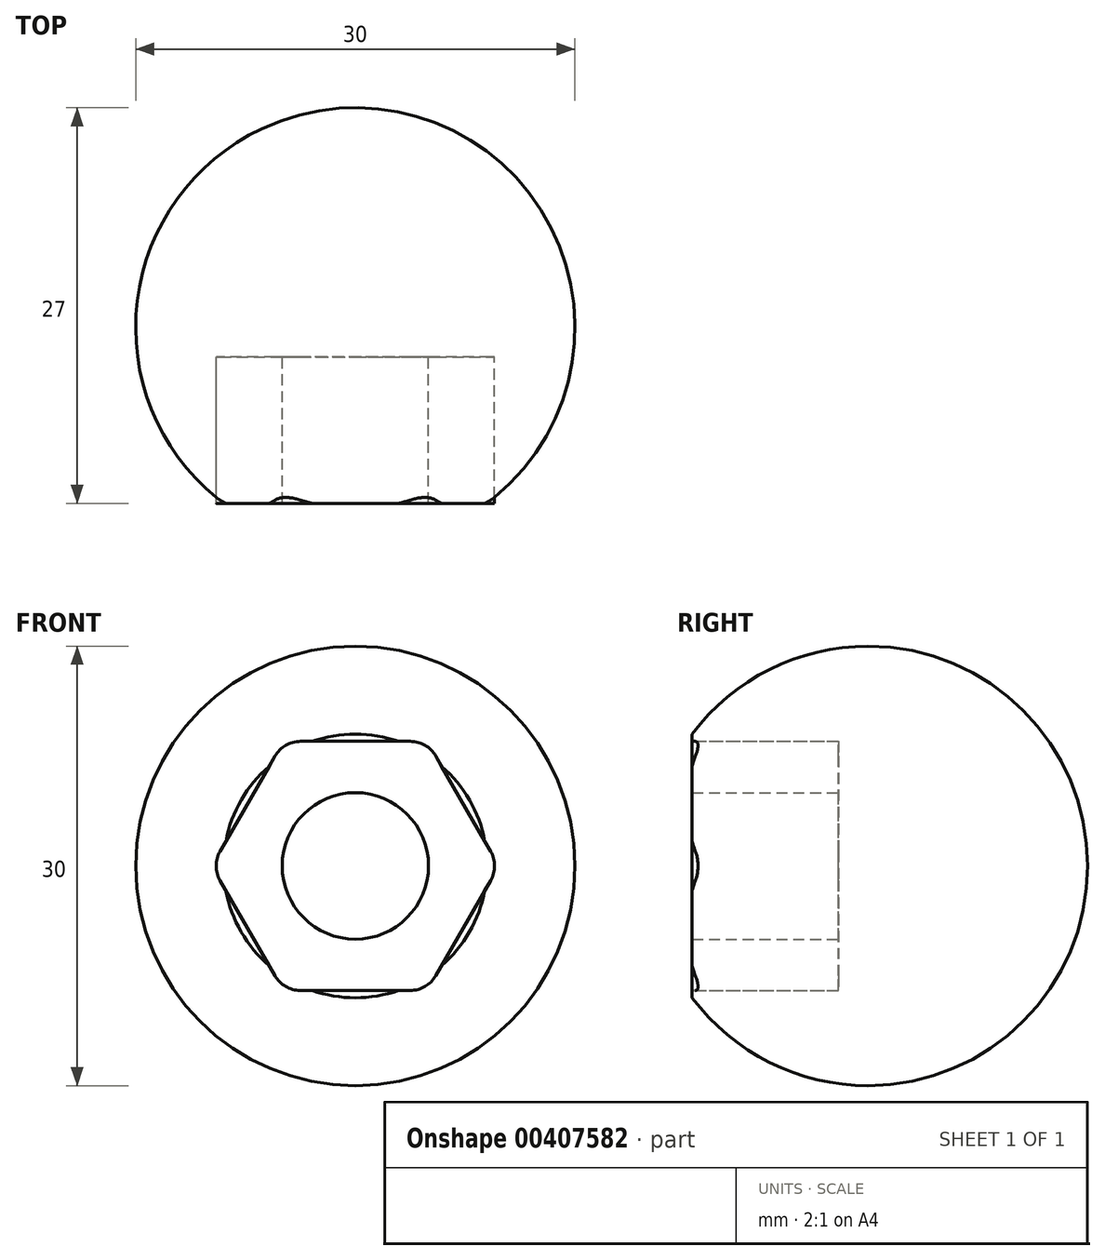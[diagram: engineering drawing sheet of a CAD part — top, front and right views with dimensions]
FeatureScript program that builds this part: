
annotation { "Feature Type Name" : "Feature", "Feature Type Description" : "" }
export const myFeature = defineFeature(function(context is Context, id is Id, definition is map)
    precondition{}
    {
        {
            var Q0;
            Q0=qCreatedBy(makeId("Front.planeOp"),FACE);
            var sketch = newSketch(context, id + "F0", { "sketchPlane" : qUnion([Q0])});
            skLineSegment(sketch, "E0", {"start": v(0, 17.98) * mm, "end": v(0, -21.13) * mm, "construction": true});
            skArc(sketch, "E1", {"start": v(0, 15) * mm, "mid": v(-15, 0) * mm, "end": v(0, -15) * mm});
            skLineSegment(sketch, "E2", {"start": v(0, -15) * mm, "end": v(0, 15) * mm});
            skSolve(sketch);
        }
        {
            var Q0;
            Q0=makeQuery(id+"F0.imprint","IMPRINT",FACE,{"disambiguationData":[TD([[makeQuery(id+"F0.imprint","IMPRINT",EDGE,{"derivedFrom":sQuery(id+"F0.wireOp",EDGE,"E1")}),1.0]])]});
            var Q1;
            Q1=sQuery(id+"F0.wireOp",EDGE,"E0");
            revolve(context, id + "F1", {"surfaceOperationType" : NewSurfaceOperationType.NEW, "entities" : qUnion([Q0]), "axis" : qUnion([Q1]), "revolveType" : RevolveType.FULL});
        }
        {
            var Q0;
            Q0=qCreatedBy(makeId("Front.planeOp"),FACE);
            var sketch = newSketch(context, id + "F2", { "sketchPlane" : qUnion([Q0])});
            skCircle(sketch, "E3.cCircle", {"center": v(0, 0) * mm, "radius": 8.5 * mm, "construction": true});
            skLineSegment(sketch, "E3.0", {"start": v(5.49, 7.5) * mm, "end": v(9.24, 1) * mm});
            skLineSegment(sketch, "E3.1", {"start": v(9.24, -1) * mm, "end": v(5.48, -7.5) * mm});
            skLineSegment(sketch, "E3.2", {"start": v(3.75, -8.5) * mm, "end": v(-3.76, -8.5) * mm});
            skLineSegment(sketch, "E3.3", {"start": v(-5.49, -7.5) * mm, "end": v(-9.24, -1) * mm});
            skLineSegment(sketch, "E3.4", {"start": v(-9.24, 1) * mm, "end": v(-5.48, 7.5) * mm});
            skLineSegment(sketch, "E3.5", {"start": v(-3.75, 8.5) * mm, "end": v(3.76, 8.5) * mm});
            skPoint(sketch, "E3.0.midPoint", {"position": v(7.36, 4.25) * mm});
            skCircle(sketch, "E4", {"center": v(0, 0) * mm, "radius": 5 * mm});
            skPoint(sketch, "E5.visualSharp", {"position": v(-4.9, 8.5) * mm});
            skArc(sketch, "E5.filletArc", {"start": v(-3.75, 8.5) * mm, "mid": v(-4.75, 8.23) * mm, "end": v(-5.48, 7.5) * mm});
            skPoint(sketch, "E6.visualSharp", {"position": v(4.91, 8.5) * mm});
            skArc(sketch, "E6.filletArc", {"start": v(5.49, 7.5) * mm, "mid": v(4.76, 8.23) * mm, "end": v(3.76, 8.5) * mm});
            skPoint(sketch, "E7.visualSharp", {"position": v(9.81, 0) * mm});
            skArc(sketch, "E7.filletArc", {"start": v(9.24, -1) * mm, "mid": v(9.5, 0) * mm, "end": v(9.24, 1) * mm});
            skPoint(sketch, "E8.visualSharp", {"position": v(4.9, -8.5) * mm});
            skArc(sketch, "E8.filletArc", {"start": v(3.75, -8.5) * mm, "mid": v(4.75, -8.23) * mm, "end": v(5.48, -7.5) * mm});
            skPoint(sketch, "E9.visualSharp", {"position": v(-4.91, -8.5) * mm});
            skArc(sketch, "E9.filletArc", {"start": v(-5.49, -7.5) * mm, "mid": v(-4.76, -8.23) * mm, "end": v(-3.76, -8.5) * mm});
            skPoint(sketch, "E10.visualSharp", {"position": v(-9.81, 0) * mm});
            skArc(sketch, "E10.filletArc", {"start": v(-9.24, 1) * mm, "mid": v(-9.5, 0) * mm, "end": v(-9.24, -1) * mm});
            skSolve(sketch);
        }
        {
            var Q0;
            Q0=makeQuery(id+"F2.imprint","IMPRINT",FACE,{"disambiguationData":[TD([[makeQuery(id+"F2.imprint","IMPRINT",EDGE,{"derivedFrom":sQuery(id+"F2.wireOp",EDGE,"E3.0")}),-1.0]])]});
            extrude(context, id + "F3", {"entities" : qUnion([Q0]), "depth" : 12 * mm, "offsetDistance" : 25 * mm, "hasSecondDirection" : true, "secondDirectionOppositeDirection" : false, "secondDirectionDepth" : 2 * mm});
        }
        {
            var Q0;
            Q0=makeQuery(id+"F3.opExtrude","CAP_FACE",FACE,{"disambiguationData":[OSD([sQuery(id+"F2.wireOp",EDGE,"E3.0"),sQuery(id+"F2.wireOp",EDGE,"E3.1"),sQuery(id+"F2.wireOp",EDGE,"E3.2"),sQuery(id+"F2.wireOp",EDGE,"E3.3"),sQuery(id+"F2.wireOp",EDGE,"E3.4"),sQuery(id+"F2.wireOp",EDGE,"E3.5"),sQuery(id+"F2.wireOp",EDGE,"E4"),sQuery(id+"F2.wireOp",EDGE,"E5.filletArc"),sQuery(id+"F2.wireOp",EDGE,"E6.filletArc"),sQuery(id+"F2.wireOp",EDGE,"E7.filletArc"),sQuery(id+"F2.wireOp",EDGE,"E8.filletArc"),sQuery(id+"F2.wireOp",EDGE,"E9.filletArc"),sQuery(id+"F2.wireOp",EDGE,"E10.filletArc")])],"isStart":false});
            var sketch = newSketch(context, id + "F4", { "sketchPlane" : qUnion([Q0])});
            skLineSegment(sketch, "E11.bottom", {"start": v(-22.5, 22.5) * mm, "end": v(22.5, 22.5) * mm});
            skLineSegment(sketch, "E11.top", {"start": v(-22.5, -22.5) * mm, "end": v(22.5, -22.5) * mm});
            skLineSegment(sketch, "E11.left", {"start": v(-22.5, 22.5) * mm, "end": v(-22.5, -22.5) * mm});
            skLineSegment(sketch, "E11.right", {"start": v(22.5, 22.5) * mm, "end": v(22.5, -22.5) * mm});
            skSolve(sketch);
        }
        {
            var Q0;
            Q0=makeQuery(id+"F4.imprint","IMPRINT",FACE,{"disambiguationData":[TD([[makeQuery(id+"F4.imprint","IMPRINT",EDGE,{"derivedFrom":sQuery(id+"F4.wireOp",EDGE,"E11.bottom")}),-1.0]])]});
            var Q1;
            Q1=makeQuery(id+"F4.imprint","IMPRINT",FACE,{"disambiguationData":[TD([[makeQuery(id+"F4.imprint","IMPRINT",EDGE,{"derivedFrom":makeQuery(id+"F3.opExtrude","CAP_EDGE",EDGE,{"disambiguationData":[OSD([sQuery(id+"F2.wireOp",EDGE,"E3.0")])],"isStart":false})}),-1.0]])]});
            extrude(context, id + "F5", {"entities" : qUnion([Q0, Q1]), "operationType" : NewBodyOperationType.REMOVE, "depth" : 25 * mm, "offsetDistance" : 25 * mm});
        }
        {
            var Q0;
            Q0=makeQuery(id+"F3.opExtrude","SWEPT_BODY",BODY,{"disambiguationData":[OSD([sQuery(id+"F2.wireOp",EDGE,"E3.0"),sQuery(id+"F2.wireOp",EDGE,"E3.1"),sQuery(id+"F2.wireOp",EDGE,"E3.2"),sQuery(id+"F2.wireOp",EDGE,"E3.3"),sQuery(id+"F2.wireOp",EDGE,"E3.4"),sQuery(id+"F2.wireOp",EDGE,"E3.5"),sQuery(id+"F2.wireOp",EDGE,"E4"),sQuery(id+"F2.wireOp",EDGE,"E5.filletArc"),sQuery(id+"F2.wireOp",EDGE,"E6.filletArc"),sQuery(id+"F2.wireOp",EDGE,"E7.filletArc"),sQuery(id+"F2.wireOp",EDGE,"E8.filletArc"),sQuery(id+"F2.wireOp",EDGE,"E9.filletArc"),sQuery(id+"F2.wireOp",EDGE,"E10.filletArc")])]});
            var Q1;
            Q1=makeQuery(id+"F1.opRevolve","SWEPT_BODY",BODY,{"disambiguationData":[OSD([sQuery(id+"F0.wireOp",EDGE,"E1"),sQuery(id+"F0.wireOp",EDGE,"E2")])]});
            booleanBodies(context, id + "F6", {"operationType" : BooleanOperationType.SUBTRACTION, "tools" : qUnion([Q0]), "targets" : qUnion([Q1]), "keepTools" : true});
        }
        {
            var Q0;
            Q0=makeQuery(id+"F3.opExtrude","CAP_FACE",FACE,{"disambiguationData":[OSD([sQuery(id+"F2.wireOp",EDGE,"E3.0"),sQuery(id+"F2.wireOp",EDGE,"E3.1"),sQuery(id+"F2.wireOp",EDGE,"E3.2"),sQuery(id+"F2.wireOp",EDGE,"E3.3"),sQuery(id+"F2.wireOp",EDGE,"E3.4"),sQuery(id+"F2.wireOp",EDGE,"E3.5"),sQuery(id+"F2.wireOp",EDGE,"E4"),sQuery(id+"F2.wireOp",EDGE,"E5.filletArc"),sQuery(id+"F2.wireOp",EDGE,"E6.filletArc"),sQuery(id+"F2.wireOp",EDGE,"E7.filletArc"),sQuery(id+"F2.wireOp",EDGE,"E8.filletArc"),sQuery(id+"F2.wireOp",EDGE,"E9.filletArc"),sQuery(id+"F2.wireOp",EDGE,"E10.filletArc")])],"isStart":false});
            var sketch = newSketch(context, id + "F7", { "sketchPlane" : qUnion([Q0])});
            skCircle(sketch, "E12", {"center": v(0, 0) * mm, "radius": 5 * mm});
            skSolve(sketch);
        }
        {
            var Q0;
            Q0 = qSketchRegion(id + "F7", true);
            extrude(context, id + "F8", {"entities" : qUnion([Q0]), "operationType" : NewBodyOperationType.REMOVE, "oppositeDirection" : true, "depth" : 20 * mm, "offsetDistance" : 25 * mm, "symmetric" : true});
        }
    });
